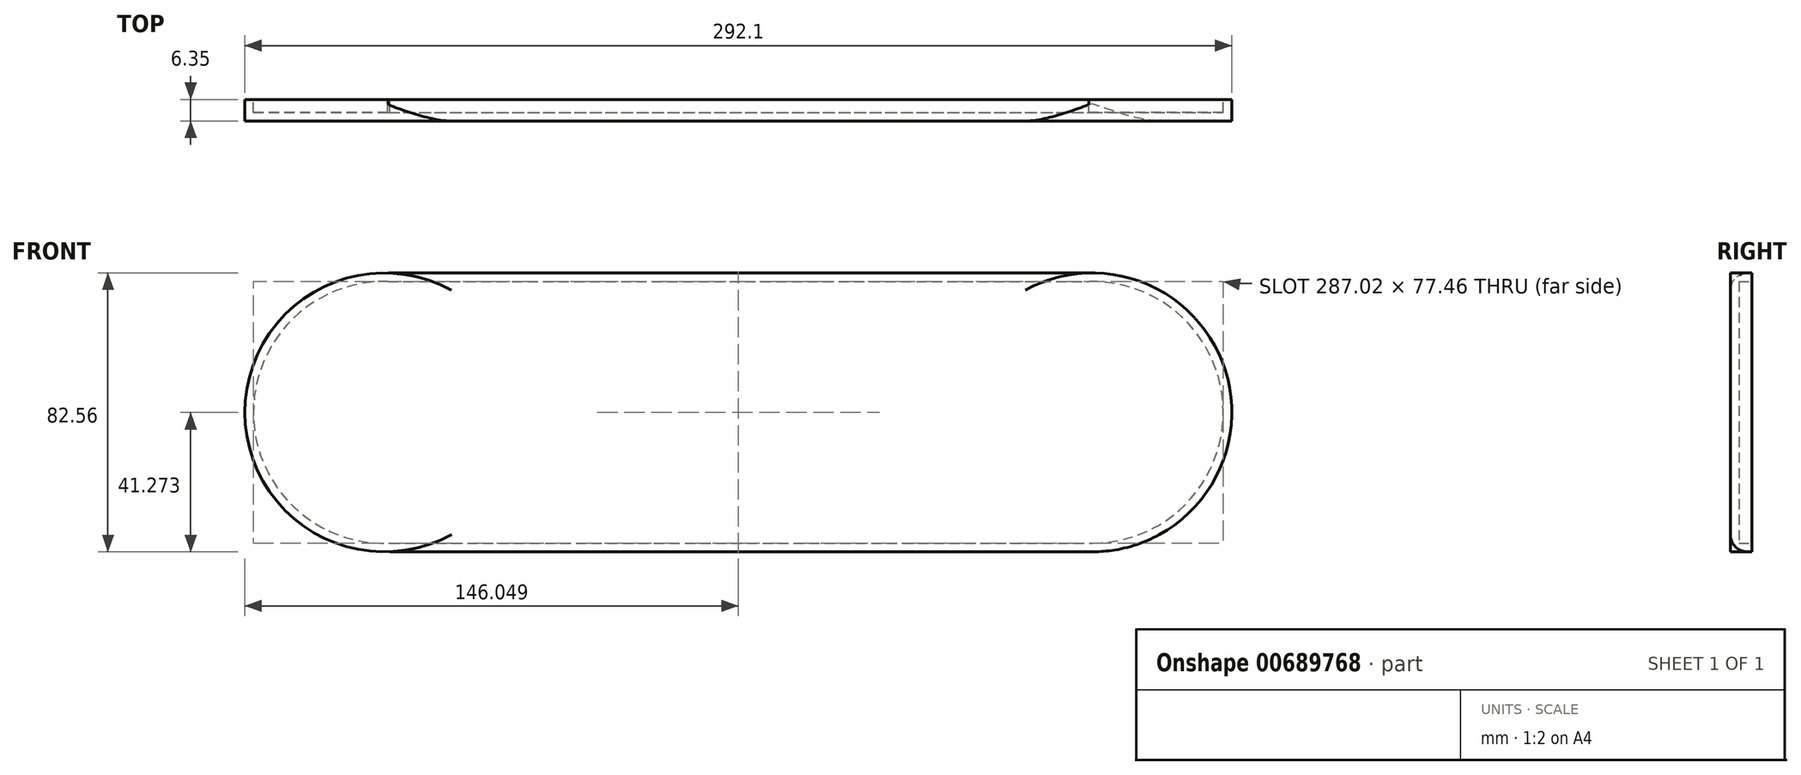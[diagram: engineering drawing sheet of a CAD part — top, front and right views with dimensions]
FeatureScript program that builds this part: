
annotation { "Feature Type Name" : "Feature", "Feature Type Description" : "" }
export const myFeature = defineFeature(function(context is Context, id is Id, definition is map)
    precondition{}
    {
        {
            var Q0;
            Q0=qCreatedBy(makeId("Front.planeOp"),FACE);
            var sketch = newSketch(context, id + "F0", { "sketchPlane" : qUnion([Q0])});
            skCircle(sketch, "E0", {"center": v(-17.74, 0) * mm, "radius": 41.28 * mm});
            skCircle(sketch, "E1", {"center": v(191.8, 0) * mm, "radius": 41.28 * mm});
            skLineSegment(sketch, "E2", {"start": v(-16.67, 41.26) * mm, "end": v(190.73, 41.26) * mm});
            skLineSegment(sketch, "E3", {"start": v(-16.1, -41.24) * mm, "end": v(190.73, -41.27) * mm});
            skLineSegment(sketch, "E4", {"start": v(-16.1, -41.24) * mm, "end": v(190.73, 41.26) * mm});
            skLineSegment(sketch, "E5", {"start": v(190.73, -41.27) * mm, "end": v(-16.67, 41.26) * mm});
            skSolve(sketch);
        }
        {
            var Q0;
            {var subQ0=sQuery(id+"F0.wireOp",EDGE,"E5");var subQ1=sQuery(id+"F0.wireOp",EDGE,"E0");var subQ5=makeQuery(id+"F0.imprint","INTERSECT",VERTEX,{"derivedFrom":[subQ1,subQ0]});Q0=makeQuery(id+"F0.imprint","IMPRINT",FACE,{"disambiguationData":[TD([[makeQuery(id+"F0.imprint","IMPRINT",EDGE,{"disambiguationData":[TD([[subQ5,1.0]])],"derivedFrom":subQ1}),1.0]])]});}
            var Q1;
            {var subQ5=sQuery(id+"F0.wireOp",EDGE,"E2");Q1=makeQuery(id+"F0.imprint","IMPRINT",FACE,{"disambiguationData":[TD([[makeQuery(id+"F0.imprint","IMPRINT",EDGE,{"derivedFrom":subQ5}),-1.0]])]});}
            var Q2;
            {var subQ0=sQuery(id+"F0.wireOp",EDGE,"E5");var subQ1=sQuery(id+"F0.wireOp",EDGE,"E0");var subQ2=makeQuery(id+"F0.imprint","INTERSECT",VERTEX,{"derivedFrom":[subQ1,subQ0]});Q2=makeQuery(id+"F0.imprint","IMPRINT",FACE,{"disambiguationData":[TD([[makeQuery(id+"F0.imprint","IMPRINT",EDGE,{"disambiguationData":[TD([[subQ2,1.0]])],"derivedFrom":subQ1}),-1.0]])]});}
            var Q3;
            {var subQ0=sQuery(id+"F0.wireOp",EDGE,"E4");var subQ1=sQuery(id+"F0.wireOp",EDGE,"E1");var subQ2=makeQuery(id+"F0.imprint","INTERSECT",VERTEX,{"derivedFrom":[subQ1,subQ0]});Q3=makeQuery(id+"F0.imprint","IMPRINT",FACE,{"disambiguationData":[TD([[makeQuery(id+"F0.imprint","IMPRINT",EDGE,{"disambiguationData":[TD([[subQ2,-1.0]])],"derivedFrom":subQ1}),-1.0]])]});}
            var Q4;
            {var subQ0=sQuery(id+"F0.wireOp",EDGE,"E4");var subQ1=sQuery(id+"F0.wireOp",EDGE,"E1");var subQ2=makeQuery(id+"F0.imprint","INTERSECT",VERTEX,{"derivedFrom":[subQ1,subQ0]});Q4=makeQuery(id+"F0.imprint","IMPRINT",FACE,{"disambiguationData":[TD([[makeQuery(id+"F0.imprint","IMPRINT",EDGE,{"disambiguationData":[TD([[subQ2,-1.0]])],"derivedFrom":subQ1}),1.0]])]});}
            var Q5;
            {var subQ0=sQuery(id+"F0.wireOp",EDGE,"E5");var subQ1=sQuery(id+"F0.wireOp",EDGE,"E0");var subQ3=makeQuery(id+"F0.imprint","INTERSECT",VERTEX,{"derivedFrom":[subQ1,subQ0]});Q5=makeQuery(id+"F0.imprint","IMPRINT",FACE,{"disambiguationData":[TD([[makeQuery(id+"F0.imprint","IMPRINT",EDGE,{"disambiguationData":[TD([[subQ3,-1.0]])],"derivedFrom":subQ1}),1.0]])]});}
            var Q6;
            {var subQ0=sQuery(id+"F0.wireOp",EDGE,"E4");var subQ1=sQuery(id+"F0.wireOp",EDGE,"E0");var subQ3=makeQuery(id+"F0.imprint","INTERSECT",VERTEX,{"derivedFrom":[subQ1,subQ0]});Q6=makeQuery(id+"F0.imprint","IMPRINT",FACE,{"disambiguationData":[TD([[makeQuery(id+"F0.imprint","IMPRINT",EDGE,{"disambiguationData":[TD([[subQ3,1.0]])],"derivedFrom":subQ1}),1.0]])]});}
            var Q7;
            {var subQ0=sQuery(id+"F0.wireOp",EDGE,"E3");Q7=makeQuery(id+"F0.imprint","IMPRINT",FACE,{"disambiguationData":[TD([[makeQuery(id+"F0.imprint","IMPRINT",EDGE,{"derivedFrom":subQ0}),1.0]])]});}
            var Q8;
            {var subQ0=sQuery(id+"F0.wireOp",EDGE,"E5");var subQ1=sQuery(id+"F0.wireOp",EDGE,"E1");var subQ2=makeQuery(id+"F0.imprint","INTERSECT",VERTEX,{"disambiguationData":[OD(0.0)],"derivedFrom":[subQ1,subQ0]});Q8=makeQuery(id+"F0.imprint","IMPRINT",FACE,{"disambiguationData":[TD([[makeQuery(id+"F0.imprint","IMPRINT",EDGE,{"disambiguationData":[TD([[subQ2,1.0]])],"derivedFrom":subQ1}),1.0]])]});}
            var Q9;
            {var subQ0=sQuery(id+"F0.wireOp",EDGE,"E4");var subQ1=sQuery(id+"F0.wireOp",EDGE,"E1");var subQ3=makeQuery(id+"F0.imprint","INTERSECT",VERTEX,{"derivedFrom":[subQ1,subQ0]});Q9=makeQuery(id+"F0.imprint","IMPRINT",FACE,{"disambiguationData":[TD([[makeQuery(id+"F0.imprint","IMPRINT",EDGE,{"disambiguationData":[TD([[subQ3,1.0]])],"derivedFrom":subQ1}),1.0]])]});}
            extrude(context, id + "F1", {"entities" : qUnion([Q0, Q1, Q2, Q3, Q4, Q5, Q6, Q7, Q8, Q9]), "depth" : 6.35 * mm, "offsetDistance" : 25.4 * mm});
        }
        {
            var Q0;
            Q0=makeQuery(id+"F1.opExtrude","CAP_FACE",FACE,{"disambiguationData":[OSD([sQuery(id+"F0.wireOp",EDGE,"E0"),sQuery(id+"F0.wireOp",EDGE,"E1"),sQuery(id+"F0.wireOp",EDGE,"E2"),sQuery(id+"F0.wireOp",EDGE,"E3"),sQuery(id+"F0.wireOp",EDGE,"E5")])],"isStart":true});
            shell(context, id + "F2", {"entities" : qUnion([Q0]), "thickness" : 2.54 * mm});
        }
        {
            var Q0;
            Q0=makeQuery(id+"F1.opExtrude","CAP_EDGE",EDGE,{"disambiguationData":[OSD([sQuery(id+"F0.wireOp",EDGE,"E2")])],"isStart":false});
            var Q1;
            Q1=makeQuery(id+"F1.opExtrude","CAP_EDGE",EDGE,{"disambiguationData":[OSD([sQuery(id+"F0.wireOp",EDGE,"E3")])],"isStart":false});
            fillet(context, id + "F3", {"entities" : qUnion([Q0, Q1]), "radius" : 5.08 * mm, "tangentPropagation" : true, "allowEdgeOverflow" : false});
        }
    });
